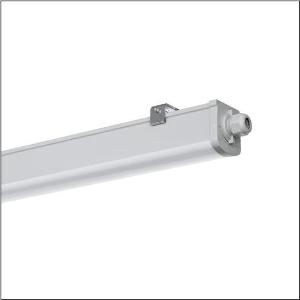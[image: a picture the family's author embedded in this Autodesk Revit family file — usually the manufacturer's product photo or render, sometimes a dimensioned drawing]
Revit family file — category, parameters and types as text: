
# Revit family: monsun_r__31_51fa207k450b_1d2e
name_source: partatom
category: Lighting Fixtures
units: mm (PartAtom-declared; Revit-internal decimal feet)

## family parameters
Cut with Voids When Loaded = No
Host = Face
Light Source = No
Part Type = Normal
Room Calculation Point = No
Round Connector Dimension = Use Diameter
Shared = No

## types (1)
- Monsun® 31 (1 x LED, 5100 lm, 38 W, 4000K)
    Apparent Load = 38 VA
    CIE Flux Codes = 42 72 91 92 100
    Color Rendering = 80
    Color Temperature = 4000K
    Default Elevation = 1800 mm
    Description = Monsun® 31, damp-proof luminaire, primary optical cover: diffuser, of PC, frosted, light emission: direct distribution, primary light characteristic: symmetric, installation type: surface-mounted, LED, rated luminous flux: 5.100lm, luminous efficacy: 134lm/W, light colour: 840, colour temperature: 4000K, control gear: ECG, with terminal, 3+1-pole, max. 2.5mm², through-wiring: 3x 2.5mm² + 1x 1.5mm², mains connection: 220..240V, AC, 50/60Hz, rated input power: 38W, housing, luminaire housing, of PC, light grey (RAL 7035), length: 1.158mm, width: 68mm, height: 76mm, protection rating (complete): IP66, insulation class (complete): insulation class II (safety insulation), certification: CE, ENEC, UKCA, protection symbol: D, impact resistance: IK08, permissible operating ambient temperature: -20..+40°C, corresponds to IFS (International Featured Standards) requirements for safety and quality in the food industry, contact your sales advisor before using the luminaires in applications with unclear chemical exposure, large temperature fluctuations or condensation-forming humidity, packaging unit: 1 piece
    Height = 77 mm
    Lamp = 1 x LED
    Lamp Light Flux = 5100 lm
    Lamp Power = 38 W
    Lamp count = 1
    Length = 1218 mm
    Luminous efficacy = 134 lm/W
    Manufacturer = Siteco
    ModVariant = No
    Model = 51FA207K450B
    Mounting Place = Ceiling
    Mounting Type = Surface mounted
    Number of Poles = 1
    OnlyDefault = Yes
    Power Factor = 1
    Product Name = Monsun® 31
    Product group = damp-proof luminaire
    ProductGroupID = 300
    Protection Class = Protection class II
    Protection Degree = IP 66
    RLX_Detail_Level = 1
    RLX_Emergency_Light_Flux = 0 lm
    RLX_Emergency_Type = 0
    RLX_Emergency_Type_DB = No
    RlxData = <blob elided: 32689 chars, md5=85ed5104>
    Socket = socket
    Standby Power = 0 W
    System Light Flux = 5100 lm
    System Power = 38 W
    Type Comments = Product without accessories
    Type Image = l_1006174.jpg
    URL = http://relux.com
    VarID = ---
    Voltage = 0 V
    Weight = 0.00 kg
    Width = 69 mm

## geometry (parser evidence)
native form markers: Blend x4, Sweep x11
no freeform markers — native parametric forms only
